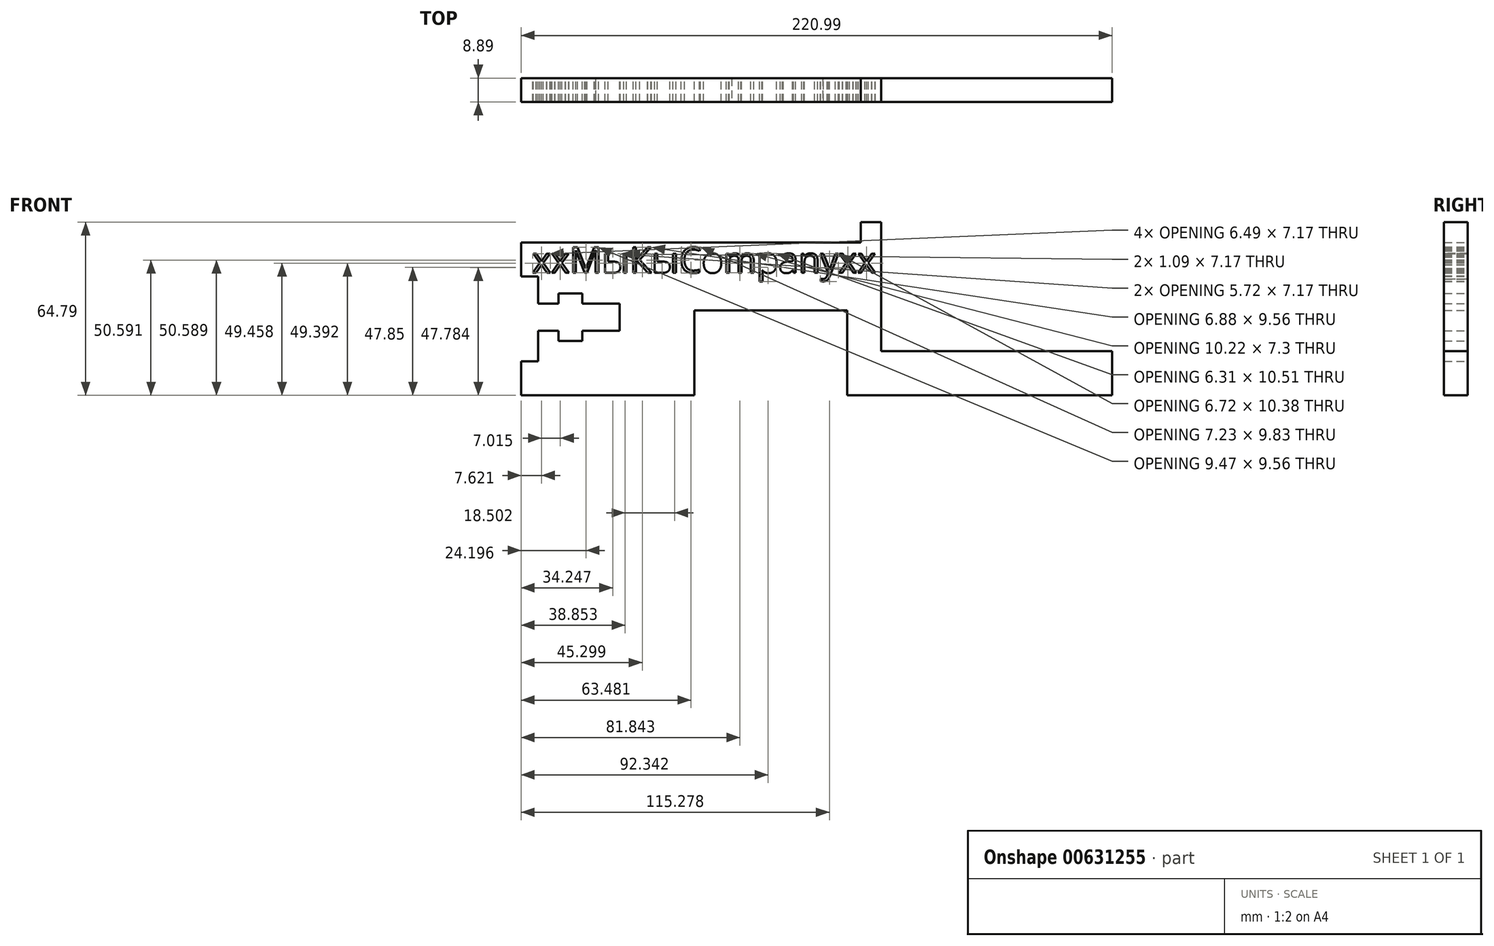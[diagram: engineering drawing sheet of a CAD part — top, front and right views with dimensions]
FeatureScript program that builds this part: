
annotation { "Feature Type Name" : "Feature", "Feature Type Description" : "" }
export const myFeature = defineFeature(function(context is Context, id is Id, definition is map)
    precondition{}
    {
        {
            var Q0;
            Q0=qCreatedBy(makeId("Front.planeOp"),FACE);
            var sketch = newSketch(context, id + "F0", { "sketchPlane" : qUnion([Q0])});
            skLineSegment(sketch, "E0", {"start": v(0, 0) * mm, "end": v(-63.51, 0) * mm});
            skLineSegment(sketch, "E1", {"start": v(0, 0) * mm, "end": v(0, 31.77) * mm});
            skLineSegment(sketch, "E2", {"start": v(0, 31.77) * mm, "end": v(57.16, 31.77) * mm});
            skLineSegment(sketch, "E3", {"start": v(57.16, 31.77) * mm, "end": v(57.16, 0) * mm});
            skLineSegment(sketch, "E4", {"start": v(57.16, 0) * mm, "end": v(156.22, 0) * mm});
            skLineSegment(sketch, "E5", {"start": v(156.22, 0) * mm, "end": v(156.22, 16.5) * mm});
            skLineSegment(sketch, "E6", {"start": v(156.22, 16.5) * mm, "end": v(69.86, 16.5) * mm});
            skLineSegment(sketch, "E7", {"start": v(69.86, 16.5) * mm, "end": v(69.86, 64.79) * mm});
            skLineSegment(sketch, "E8", {"start": v(69.86, 64.79) * mm, "end": v(62.24, 64.79) * mm});
            skLineSegment(sketch, "E9", {"start": v(62.24, 64.79) * mm, "end": v(62.24, 57.17) * mm});
            skLineSegment(sketch, "E10", {"start": v(62.24, 57.17) * mm, "end": v(-64.77, 57.17) * mm});
            skLineSegment(sketch, "E11", {"start": v(-64.77, 57.17) * mm, "end": v(-64.77, 44.46) * mm});
            skLineSegment(sketch, "E12", {"start": v(-64.77, 44.46) * mm, "end": v(-58.42, 44.46) * mm});
            skLineSegment(sketch, "E13", {"start": v(-58.42, 44.46) * mm, "end": v(-58.42, 34.3) * mm});
            skLineSegment(sketch, "E14", {"start": v(-58.42, 34.3) * mm, "end": v(-50.8, 34.3) * mm});
            skLineSegment(sketch, "E15", {"start": v(-50.8, 34.3) * mm, "end": v(-50.8, 38.12) * mm});
            skLineSegment(sketch, "E16", {"start": v(-50.8, 38.12) * mm, "end": v(-41.91, 38.12) * mm});
            skLineSegment(sketch, "E17", {"start": v(-41.91, 38.12) * mm, "end": v(-41.91, 34.3) * mm});
            skLineSegment(sketch, "E18", {"start": v(-41.91, 34.3) * mm, "end": v(-27.93, 34.3) * mm});
            skLineSegment(sketch, "E19", {"start": v(-27.93, 34.3) * mm, "end": v(-27.93, 24.13) * mm});
            skLineSegment(sketch, "E20", {"start": v(-27.93, 24.13) * mm, "end": v(-41.91, 24.13) * mm});
            skLineSegment(sketch, "E21", {"start": v(-41.91, 24.13) * mm, "end": v(-41.91, 20.33) * mm});
            skLineSegment(sketch, "E22", {"start": v(-41.91, 20.33) * mm, "end": v(-50.8, 20.33) * mm});
            skLineSegment(sketch, "E23", {"start": v(-50.8, 20.33) * mm, "end": v(-50.8, 24.13) * mm});
            skLineSegment(sketch, "E24", {"start": v(-50.8, 24.13) * mm, "end": v(-58.42, 24.13) * mm});
            skLineSegment(sketch, "E25", {"start": v(-58.42, 24.13) * mm, "end": v(-58.42, 12.7) * mm});
            skLineSegment(sketch, "E26", {"start": v(-58.42, 12.7) * mm, "end": v(-64.77, 12.7) * mm});
            skLineSegment(sketch, "E27", {"start": v(-64.77, 12.7) * mm, "end": v(-64.77, 0) * mm});
            skLineSegment(sketch, "E28", {"start": v(-64.77, 0) * mm, "end": v(-63.51, 0) * mm});
            skText(sketch, "E29", { "text": "xxМыКыСompanyxx", "fontName": "OpenSans-Regular.ttf"});
            const initialGuessF0  = {"E29": [-0.06065, 0.04581, 1, 0, 0.00964]};
            skSetInitialGuess(sketch, initialGuessF0);
            skSolve(sketch);
        }
        {
            var Q0;
            Q0 = qSketchRegion(id + "F0", true);
            extrude(context, id + "F1", {"entities" : qUnion([Q0]), "depth" : 8.9 * mm, "offsetDistance" : 25.4 * mm});
        }
    });
